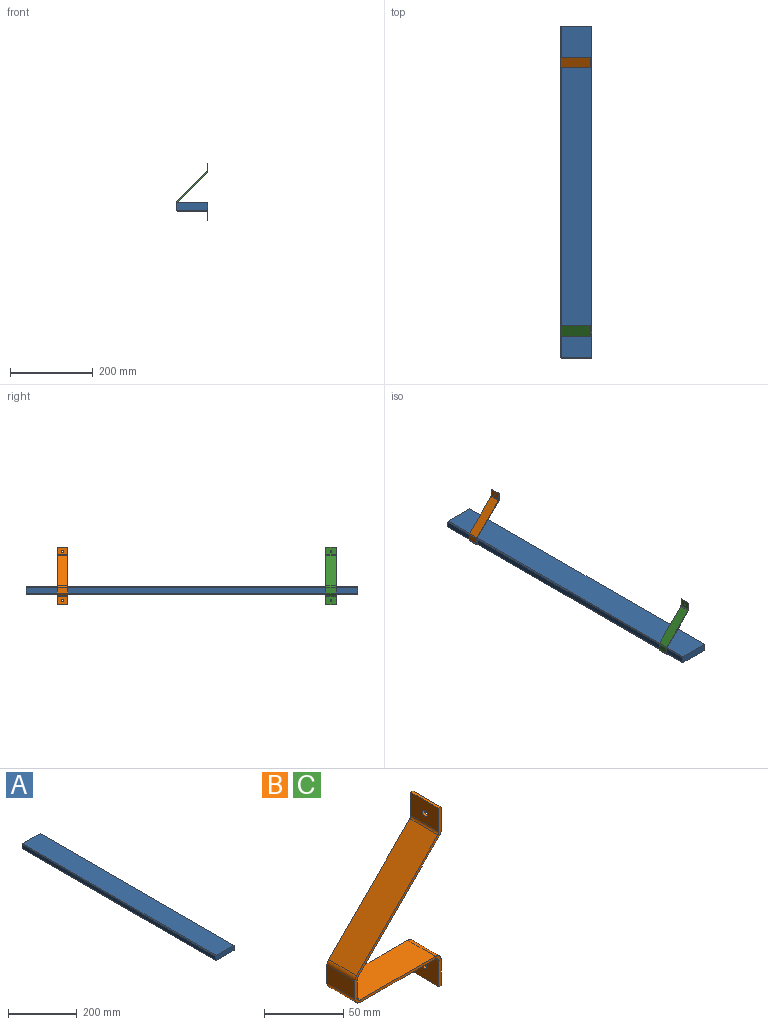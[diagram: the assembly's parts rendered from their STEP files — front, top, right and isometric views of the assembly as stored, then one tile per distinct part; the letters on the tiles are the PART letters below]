
ASSEMBLY  parts=3 mates=4
PART A: 8 faces, bbox 75x800x18 mm
  f0: plane 800x73mm, normal (0,0,-1), area 58400mm2, adj f1,f4,f5,f6
  f1: plane 800x18mm, normal (1,0,0), area 14400mm2, adj f0,f2,f4,f5
  f2: plane 800x73mm, normal (0,0,1), area 58400mm2, adj f1,f4,f5,f7
  f3: plane 800x14mm, normal (-1,0,0), area 11200mm2, adj f4,f5,f6,f7
  f4: plane 75x18mm, normal (0,-1,0), area 1346mm2, adj f0,f1,f2,f3,f6,f7
  f5: plane 75x18mm, normal (0,1,0), area 1346mm2, adj f0,f1,f2,f3,f6,f7
  f6: plane 800x2mm, normal (-0.71,0,-0.71), area 2262.7mm2, adj f0,f3,f4,f5
  f7: plane 800x2mm, normal (-0.71,0,0.71), area 2262.7mm2, adj f2,f3,f4,f5
PART B: 40 faces, bbox 77x25x138 mm
  f0: plane 20x2mm, normal (0,1,0), area 40mm2, adj f3,f4,f5,f37
  f1: plane 20x2mm, normal (0,-1,0), area 40mm2, adj f3,f4,f5,f36
  f2: cylinder r=2.25mm len=4.5mm, axis (1,0,0), area 28.3mm2, adj f4,f5
  f3: plane 25x2mm, normal (0,0,-1), area 50mm2, adj f0,f1,f4,f5
  f4: plane 25x20mm, normal (1,0,0), area 484.1mm2, adj f0,f1,f2,f3,f38
  f5: plane 25x20mm, normal (-1,0,0), area 484.1mm2, adj f0,f1,f2,f3,f39
  f6: plane 67x2mm, normal (0,1,0), area 134mm2, adj f8,f9,f33,f37
  f7: plane 67x2mm, normal (0,-1,0), area 134mm2, adj f8,f9,f32,f36
  f8: plane 67x25mm, normal (0,0,1), area 1675mm2, adj f6,f7,f35,f38
  f9: plane 67x25mm, normal (0,0,-1), area 1675mm2, adj f6,f7,f34,f39
  f10: plane 13.76x2mm, normal (0,1,0), area 27.5mm2, adj f12,f13,f29,f33
  f11: plane 13.76x2mm, normal (0,-1,0), area 27.5mm2, adj f12,f13,f28,f32
  f12: plane 25x13.76mm, normal (1,0,0), area 343.9mm2, adj f10,f11,f31,f35
  f13: plane 25x13.76mm, normal (-1,0,0), area 343.9mm2, adj f10,f11,f30,f34
  f14: plane 74.07x74.07mm, normal (0,1,0), area 205.5mm2, adj f16,f17,f25,f29
  f15: plane 74.07x74.07mm, normal (0,-1,0), area 205.5mm2, adj f16,f17,f24,f28
  f16: plane 72.66x72.66mm, normal (0.71,0,-0.71), area 2568.8mm2, adj f14,f15,f26,f31
  f17: plane 72.66x72.66mm, normal (-0.71,0,0.71), area 2568.8mm2, adj f14,f15,f27,f30
  f18: plane 17.93x2mm, normal (0,1,0), area 35.9mm2, adj f19,f22,f23,f25
  f19: plane 25x2mm, normal (0,0,1), area 50mm2, adj f18,f20,f22,f23
  f20: plane 17.93x2mm, normal (0,-1,0), area 35.9mm2, adj f19,f22,f23,f24
  f21: cylinder r=2.25mm len=4.5mm, axis (1,0,0), area 28.3mm2, adj f22,f23
  f22: plane 25x17.93mm, normal (1,0,0), area 432.3mm2, adj f18,f19,f20,f21,f26
  f23: plane 25x17.93mm, normal (-1,0,0), area 432.3mm2, adj f18,f19,f20,f21,f27
  f24: plane 3.54x2.88mm, normal (0,-1,0), area 6.3mm2, adj f15,f20,f26,f27
  f25: plane 3.54x2.88mm, normal (0,1,0), area 6.3mm2, adj f14,f18,f26,f27
  f26: cylinder r=5mm len=25mm, axis (0,-1,0), area 98.2mm2, adj f16,f22,f24,f25
  f27: cylinder r=3mm len=25mm, axis (0,-1,0), area 58.9mm2, adj f17,f23,f24,f25
  f28: plane 3.54x2.88mm, normal (0,-1,0), area 6.3mm2, adj f11,f15,f30,f31
  f29: plane 3.54x2.88mm, normal (0,1,0), area 6.3mm2, adj f10,f14,f30,f31
  f30: cylinder r=5mm len=25mm, axis (0,-1,0), area 98.2mm2, adj f13,f17,f28,f29
  f31: cylinder r=3mm len=25mm, axis (0,-1,0), area 58.9mm2, adj f12,f16,f28,f29
  f32: plane 5x5mm, normal (0,-1,0), area 12.6mm2, adj f7,f11,f34,f35
  f33: plane 5x5mm, normal (0,1,0), area 12.6mm2, adj f6,f10,f34,f35
  f34: cylinder r=5mm len=25mm, axis (0,-1,0), area 196.3mm2, adj f9,f13,f32,f33
  f35: cylinder r=3mm len=25mm, axis (0,-1,0), area 117.8mm2, adj f8,f12,f32,f33
  f36: plane 5x5mm, normal (0,-1,0), area 12.6mm2, adj f1,f7,f38,f39
  f37: plane 5x5mm, normal (0,1,0), area 12.6mm2, adj f0,f6,f38,f39
  f38: cylinder r=5mm len=25mm, axis (0,-1,0), area 196.3mm2, adj f4,f8,f36,f37
  f39: cylinder r=3mm len=25mm, axis (0,-1,0), area 117.8mm2, adj f5,f9,f36,f37
PART C: same geometry as B
PLACE A t=(-168.33,187.48,-171.74)mm fixed
PLACE B t=(-168.33,112.05,-196.74)mm
PLACE C t=(-168.33,-535,-196.74)mm
MATE planar B.f12 <-> A.f3  axis (1,0,0) through (-243.33,99.55,-161.87)mm
MATE planar B.f8 <-> A.f0  axis (0,0,1) through (-206.83,99.55,-171.74)mm
MATE planar C.f12 <-> A.f3  axis (1,0,0) through (-243.33,-547.5,-161.87)mm
MATE planar C.f8 <-> A.f0  axis (0,0,1) through (-206.83,-560,-171.74)mm
